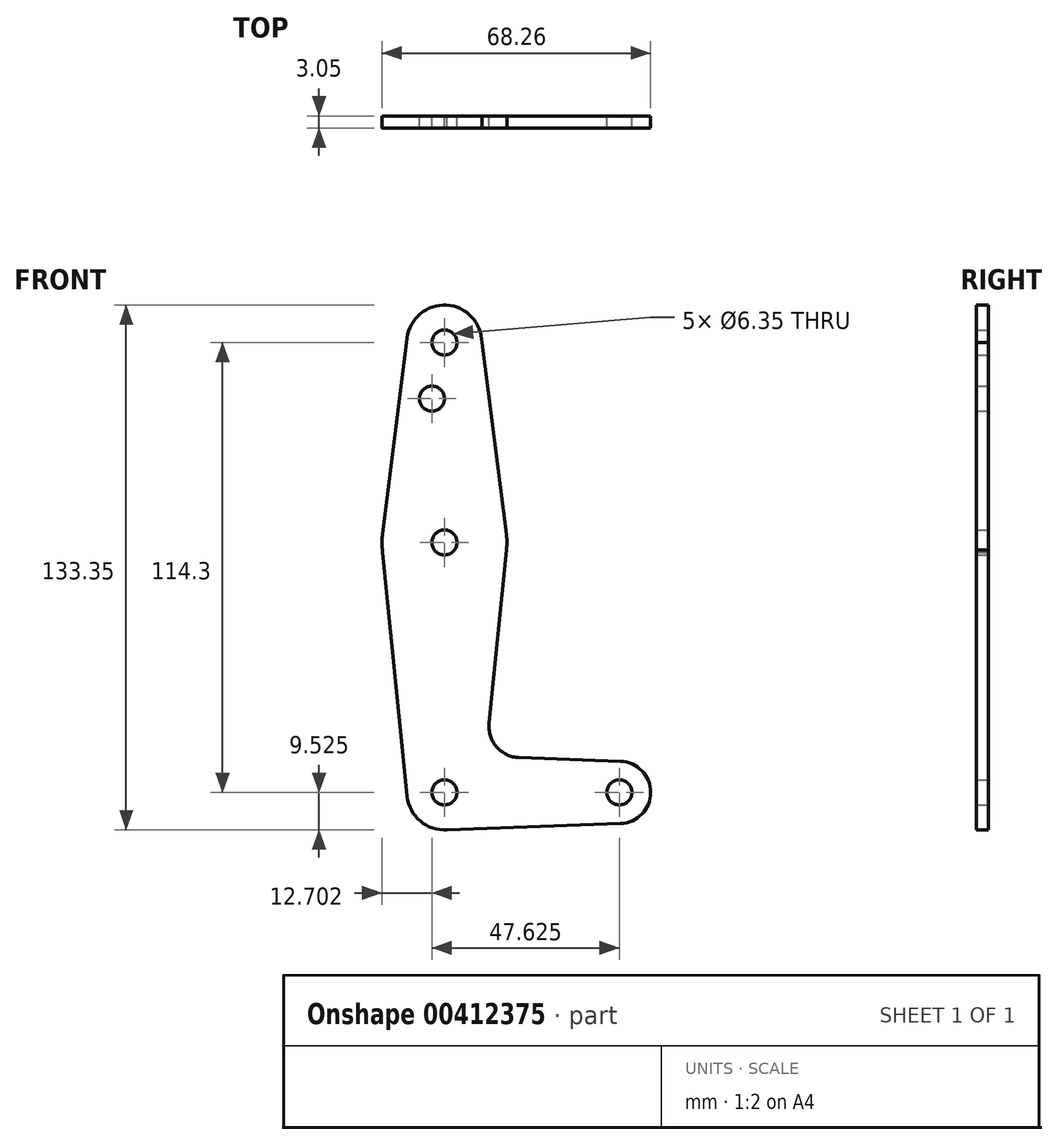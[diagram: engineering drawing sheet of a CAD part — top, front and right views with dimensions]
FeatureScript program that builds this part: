
annotation { "Feature Type Name" : "Feature", "Feature Type Description" : "" }
export const myFeature = defineFeature(function(context is Context, id is Id, definition is map)
    precondition{}
    {
        {
            var Q0;
            Q0=qCreatedBy(makeId("Front.planeOp"),FACE);
            var sketch = newSketch(context, id + "F0", { "sketchPlane" : qUnion([Q0])});
            skLineSegment(sketch, "E0", {"start": v(0, 114.3) * mm, "end": v(0, 0) * mm, "construction": true});
            skLineSegment(sketch, "E1", {"start": v(0, 0) * mm, "end": v(44.46, 0) * mm, "construction": true});
            skCircle(sketch, "E2", {"center": v(0, 114.3) * mm, "radius": 9.53 * mm});
            skCircle(sketch, "E3", {"center": v(0, 63.5) * mm, "radius": 15.88 * mm});
            skCircle(sketch, "E4", {"center": v(0, 0) * mm, "radius": 9.53 * mm});
            skCircle(sketch, "E5", {"center": v(44.46, 0) * mm, "radius": 7.94 * mm});
            skLineSegment(sketch, "E6", {"start": v(9.53, 114.28) * mm, "end": v(15.75, 65.51) * mm});
            skLineSegment(sketch, "E7", {"start": v(-9.43, 115.58) * mm, "end": v(-15.74, 65.49) * mm});
            skLineSegment(sketch, "E8", {"start": v(-15.66, 60.96) * mm, "end": v(-9.47, -0.94) * mm});
            skLineSegment(sketch, "E9", {"start": v(15.83, 62.18) * mm, "end": v(11.35, 17.6) * mm});
            skLineSegment(sketch, "E10", {"start": v(18.97, 8.85) * mm, "end": v(44.74, 7.94) * mm});
            skLineSegment(sketch, "E11", {"start": v(0, -9.52) * mm, "end": v(44.74, -7.93) * mm});
            skCircle(sketch, "E12", {"center": v(0, 114.3) * mm, "radius": 3.18 * mm});
            skCircle(sketch, "E13", {"center": v(-3.17, 100.03) * mm, "radius": 3.18 * mm});
            skCircle(sketch, "E14", {"center": v(0, 63.5) * mm, "radius": 3.18 * mm});
            skCircle(sketch, "E15", {"center": v(0, 0) * mm, "radius": 3.18 * mm});
            skCircle(sketch, "E16", {"center": v(44.46, 0) * mm, "radius": 3.18 * mm});
            skArc(sketch, "E17.filletArc", {"start": v(11.35, 17.6) * mm, "mid": v(13.27, 11.57) * mm, "end": v(18.97, 8.85) * mm});
            skSolve(sketch);
        }
        {
            var Q0;
            Q0 = qSketchRegion(id + "F0", true);
            extrude(context, id + "F1", {"entities" : qUnion([Q0]), "depth" : 3.05 * mm});
        }
    });
